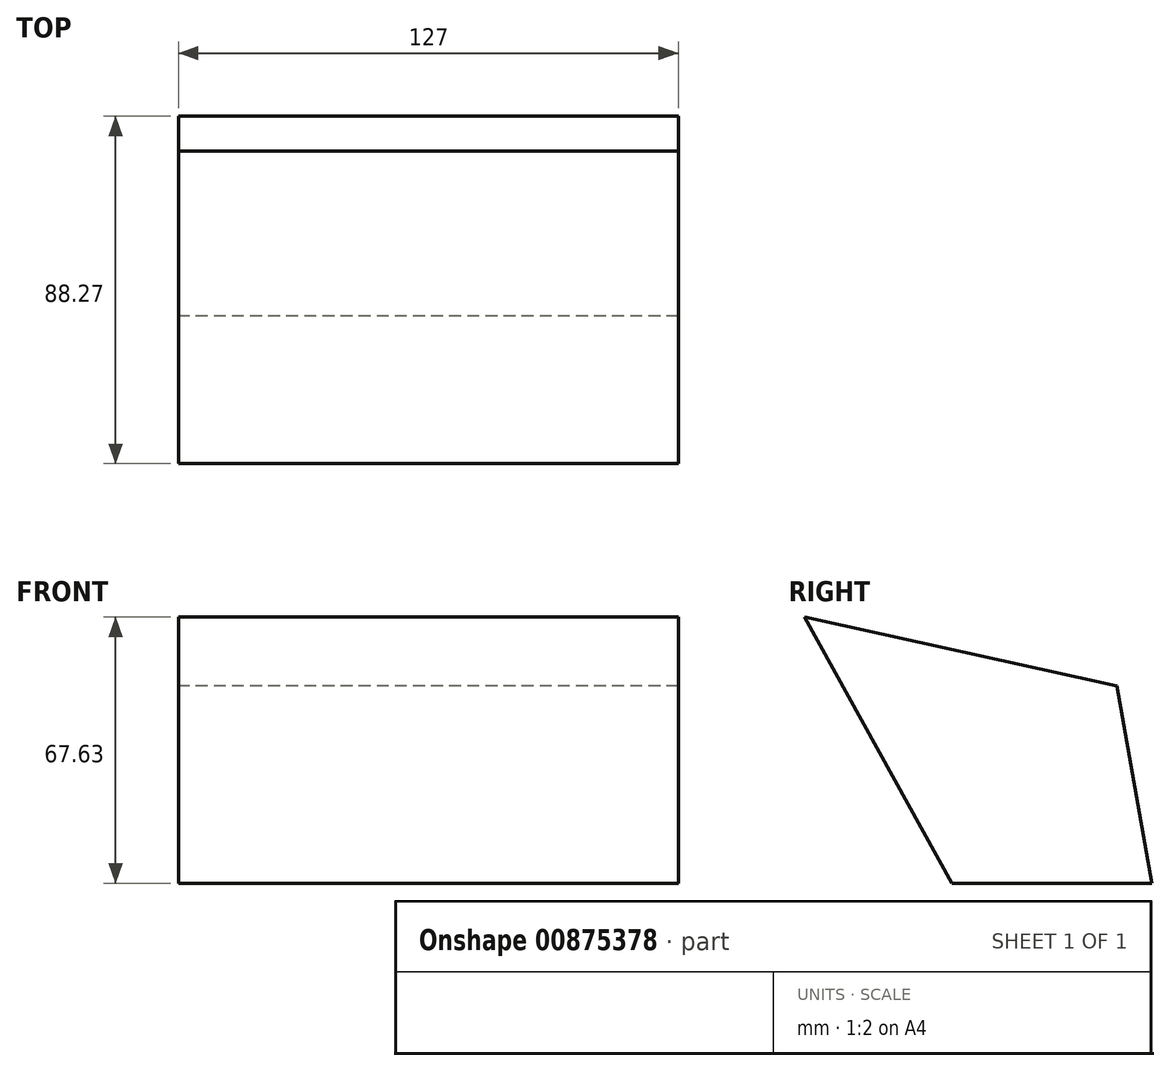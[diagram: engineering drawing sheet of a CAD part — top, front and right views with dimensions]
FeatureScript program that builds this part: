
annotation { "Feature Type Name" : "Feature", "Feature Type Description" : "" }
export const myFeature = defineFeature(function(context is Context, id is Id, definition is map)
    precondition{}
    {
        {
            var Q0;
            Q0=qCreatedBy(makeId("Right.planeOp"),FACE);
            var sketch = newSketch(context, id + "F0", { "sketchPlane" : qUnion([Q0])});
            skLineSegment(sketch, "E0", {"start": v(-45.92, 53.59) * mm, "end": v(33.44, 36.05) * mm});
            skLineSegment(sketch, "E1", {"start": v(-45.92, 53.59) * mm, "end": v(-8.47, -14.04) * mm});
            skLineSegment(sketch, "E2", {"start": v(42.35, -14.04) * mm, "end": v(33.44, 36.05) * mm});
            skLineSegment(sketch, "E3", {"start": v(-8.47, -14.04) * mm, "end": v(42.35, -14.04) * mm});
            skSolve(sketch);
        }
        {
            var Q0;
            Q0 = qSketchRegion(id + "F0", true);
            extrude(context, id + "F1", {"entities" : qUnion([Q0]), "depth" : 127 * mm, "offsetDistance" : 25.4 * mm});
        }
    });
